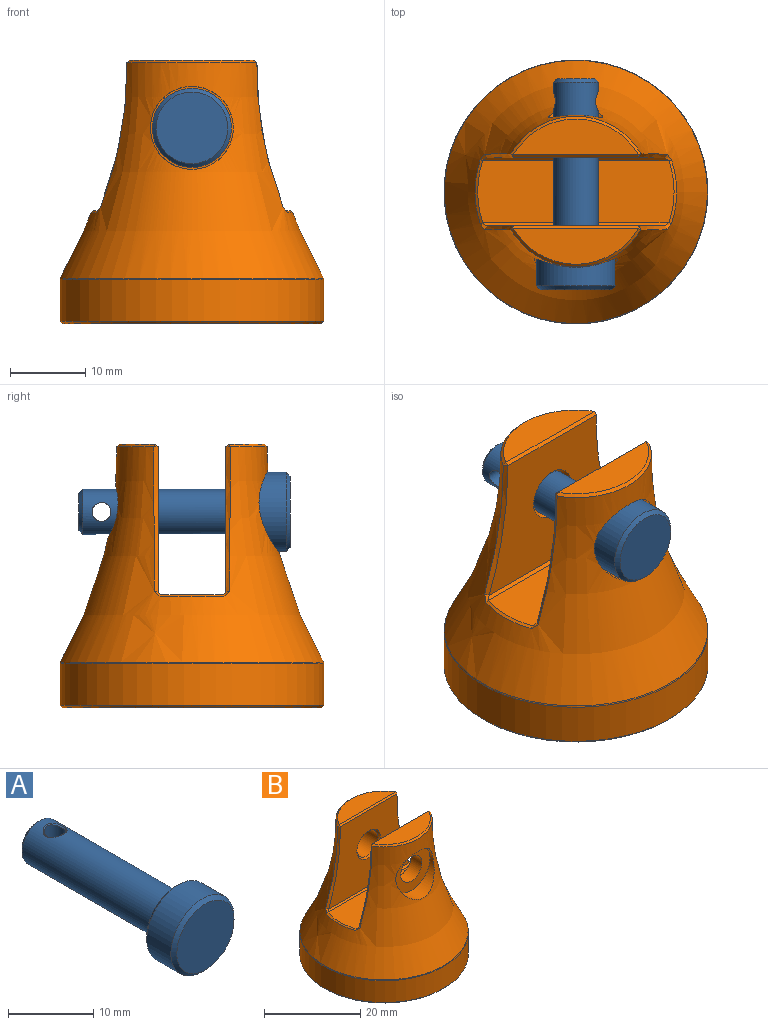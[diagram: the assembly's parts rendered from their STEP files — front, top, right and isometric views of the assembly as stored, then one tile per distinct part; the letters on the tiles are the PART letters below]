
ASSEMBLY  parts=2 mates=1
PART A: 10 faces, bbox 10.5x28x10.5 mm
  f0: cylinder r=5.25mm len=10.5mm, axis (0,1,0), area 131.9mm2, adj f6,f7
  f1: plane 9.5x9.5mm, normal (0,-1,0), area 70.9mm2, adj f6
  f2: plane 9.5x9.5mm, normal (0,1,0), area 42.6mm2, adj f3,f7
  f3: cylinder r=3mm len=22.5mm, axis (0,-1,0), area 413.1mm2, adj f2,f5,f8,f9
  f4: plane 5x5mm, normal (0,1,0), area 19.6mm2, adj f8
  f5: cylinder r=1.25mm len=5.52mm, axis (0,0,1), area 42.3mm2, adj f3,f9
  f6: cone r=4.75mm half-angle=45deg, axis (0,1,0), area 22.2mm2, adj f0,f1
  f7: cone r=5.25mm half-angle=45deg, axis (0,-1,0), area 22.2mm2, adj f0,f2
  f8: cone r=2.5mm half-angle=45deg, axis (0,-1,0), area 12.2mm2, adj f3,f4
  f9: bspline ~2.88x2.76mm, area 1.7mm2, adj f3,f5
PART B: 39 faces, bbox 56.5x56.5x78.5 mm
  f0: torus R=64.99mm, axis (0,0,-1), area 1768.4mm2, adj f14,f19,f20,f21,f23,f26,f27,f28
  f1: cylinder r=2.5mm len=14.63mm, axis (0,0,-1), area 229.8mm2, adj f6,f11
  f2: plane 16.6x4.75mm, normal (0,0,1), area 55.9mm2, adj f14,f15
  f3: cylinder r=17.5mm len=35mm, axis (0,0,-1), area 608.2mm2, adj f12,f36
  f4: plane 34.26x34.26mm, normal (0,0,-1), area 896.1mm2, adj f11,f12
  f5: plane 16.6x4.75mm, normal (0,0,1), area 55.9mm2, adj f18,f20
  f6: plane 26.05x8.26mm, normal (0,0,1), area 191.9mm2, adj f1,f22,f27,f30,f33
  f7: plane 23.98x19.66mm, normal (0,-1,0), area 324.6mm2, adj f13,f18,f28,f29,f33
  f8: plane 23.97x19.66mm, normal (0,1,0), area 324.5mm2, adj f15,f19,f21,f22,f34
  f9: cylinder r=3.1mm len=6.2mm, axis (0,-1,0), area 61mm2, adj f34,f38
  f10: cylinder r=3.1mm len=6.2mm, axis (0,-1,0), area 103.1mm2, adj f13,f35
  f11: cone r=2.5mm half-angle=45deg, axis (0,0,-1), area 8.8mm2, adj f1,f4
  f12: cone r=17.13mm half-angle=45deg, axis (0,0,1), area 56.8mm2, adj f3,f4
  f13: cone r=3.1mm half-angle=45deg, axis (0,-1,0), area 10.8mm2, adj f7,f10
  f14: cone r=9.99mm half-angle=44.5deg, axis (0,0,-1), area 10.7mm2, adj f0,f2,f16,f17
  f15: plane 16.6x0.37mm, normal (0,0.71,0.71), area 8.7mm2, adj f2,f8,f16,f17
  f16: plane 0.56x0.37mm, normal (-0.78,0.44,0.44), area 0.1mm2, adj f14,f15,f19
  f17: plane 0.56x0.38mm, normal (0.78,0.44,0.44), area 0.1mm2, adj f14,f15,f21
  f18: plane 16.61x0.37mm, normal (0,-0.71,0.71), area 8.7mm2, adj f5,f7,f24,f25
  f19: bspline ~21.77x4.69mm, area 12.3mm2, adj f0,f8,f16,f23
  f20: cone r=9.99mm half-angle=44.5deg, axis (0,0,-1), area 10.7mm2, adj f0,f5,f24,f25
  f21: bspline ~21.77x4.52mm, area 12.3mm2, adj f0,f8,f17,f26
  f22: plane 24.7x0.37mm, normal (0,0.71,0.71), area 12.6mm2, adj f6,f8,f23,f26
  f23: bspline ~0.9x0.89mm, area 0.4mm2, adj f0,f19,f22,f27
  f24: plane 0.56x0.38mm, normal (-0.78,-0.44,0.44), area 0.1mm2, adj f18,f20,f28
  f25: plane 0.56x0.38mm, normal (0.78,-0.44,0.44), area 0.1mm2, adj f18,f20,f29
  f26: bspline ~0.9x0.89mm, area 0.4mm2, adj f0,f21,f22,f30
  f27: cone r=13.37mm half-angle=55.1deg, axis (0,0,-1), area 3.6mm2, adj f0,f6,f23,f31
  f28: bspline ~21.77x4.69mm, area 12.3mm2, adj f0,f7,f24,f31
  f29: bspline ~21.77x4.52mm, area 12.3mm2, adj f0,f7,f25,f32
  f30: cone r=13.37mm half-angle=55.1deg, axis (0,0,-1), area 3.6mm2, adj f0,f6,f26,f32
  f31: bspline ~0.9x0.89mm, area 0.4mm2, adj f0,f27,f28,f33
  f32: bspline ~0.89x0.88mm, area 0.4mm2, adj f0,f29,f30,f33
  f33: plane 24.7x0.37mm, normal (0,-0.71,0.71), area 12.6mm2, adj f6,f7,f31,f32
  f34: cone r=3.47mm half-angle=45deg, axis (0,1,0), area 10.8mm2, adj f8,f9
  f35: bspline ~7.19x6.89mm, area 11.7mm2, adj f0,f10
  f36: cone r=17.5mm half-angle=15.1deg, axis (0,0,-1), area 21.1mm2, adj f0,f3
  f37: cylinder r=5.5mm len=11mm, axis (0,1,0), area 66.4mm2, adj f0,f38
  f38: plane 11x11mm, normal (0,-1,0), area 64.8mm2, adj f9,f37
PLACE A rot(axis=(0,1,0),90deg) t=(32.37,-5.49,22.29)mm
PLACE B t=(32.37,2.51,-3.71)mm
MATE fastened A.f0 <-> B.f9  axis (0,-1,0) through (32.37,-5.49,22.29)mm
